# Revit family: Дифузор_круглий_витяжний
name_source: partatom
category: Air Terminals
units: mm (PartAtom-declared; Revit-internal decimal feet)

## family parameters
Always vertical = Yes
Cut with Voids When Loaded = No
OmniClass Number = 23.75.70.21.27.11
OmniClass Title = Diffusers, Registers, and Grilles
Part Type = Normal
Room Calculation Point = No
Round Connector Dimension = Use Radius
Shared = No
Work Plane-Based = No

## types (5) — shared parameters
ADSK_Единица измерения = шт.
ADSK_Количество = 1
Max Flow = 170.0 m³/h
Min Flow = 0.0 m³/h
zero-valued in all types: Default Elevation

## per-type parameters (varying)
| type | ADSK_Марка | ADSK_Наименование | ADSK_Наименование краткое | Диаметр подключения | Наружный радиус | Отступ стрелки | Радиус вставки | Радиус подключения |
| ø250 |  | Пластиковый диффузор ø250мм. | Диффузор ø250мм. | 250 mm | 150 mm | 330 mm | 110 mm  [stored 0.360892 ft] | 125 mm  [stored 0.410105 ft] |
| ø200 |  | Пластиковый диффузор ø200мм. | Диффузор ø200мм. | 200 mm | 125 mm  [stored 0.410105 ft] | 280 mm | 85 mm  [stored 0.278871 ft] | 100 mm  [stored 0.328084 ft] |
| ø160 |  | Пластиковый диффузор ø160мм. | Диффузор ø160мм. | 160 mm | 105 mm  [stored 0.344488 ft] | 240 mm  [stored 0.787402 ft] | 65 mm  [stored 0.213255 ft] | 80 mm  [stored 0.262467 ft] |
| ø125 |  | Пластиковый диффузор ø125мм. | Диффузор ø125мм. | 125 mm | 88 mm | 205 mm | 48 mm | 63 mm |
| ø100 | KW-100 | Пластиковый диффузор ø100мм. | Диффузор ø100мм. | 100 mm | 75 mm | 180 mm | 35 mm | 50 mm  [stored 0.164042 ft] |

note: [stored X ft] marks values corroborated as IEEE doubles in the binary element streams (Revit-internal decimal feet)
